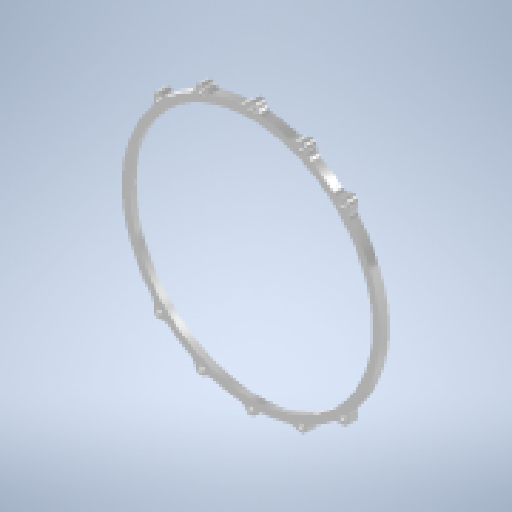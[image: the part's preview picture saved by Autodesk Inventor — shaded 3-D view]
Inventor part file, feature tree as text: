
AUTODESK INVENTOR PART (.ipt)
format: ipt  version: 2024 (Build 280153000, 153)  size: 287,232 bytes
history: native  units: mm
features: sketch x5, extrude x4, projected_geometry x3, other x1, fillet x1, pattern_circular x1, hole x1
ambient origin geometry x8: Origin, YZ Plane, XZ Plane, XY Plane, X Axis, Y Axis, Z Axis, Center Point
bodies: Body1 (feature_tree)
feature tree (16):
  other  "ソリッド1"
  extrude  "押し出し1"  Depth=122.0mm
  extrude  "押し出し2"  Depth=130.0mm
  extrude  "押し出し3"  Depth=2.5mm TaperAngle=0.0deg
  fillet  "フィレット1"  Radius=125.0mm
  pattern_circular  "円形状パターン1"  [2 undecoded]
  extrude  "押し出し4"  Depth=6.0mm
  hole  "穴1"  [1 undecoded]
  sketch  "スケッチ1"
  sketch  "スケッチ2"
  projected_geometry  "投影ループ1"
  sketch  "スケッチ3"
  projected_geometry  "投影ループ2"
  sketch  "スケッチ4"
  projected_geometry  "投影ループ3"
  sketch  "スケッチ5"
note: 3 required parameter values undecoded (feature->parameter linkage not recoverable at this tier; creation-order binding heuristic only, values carry confidence <= 0.55)
